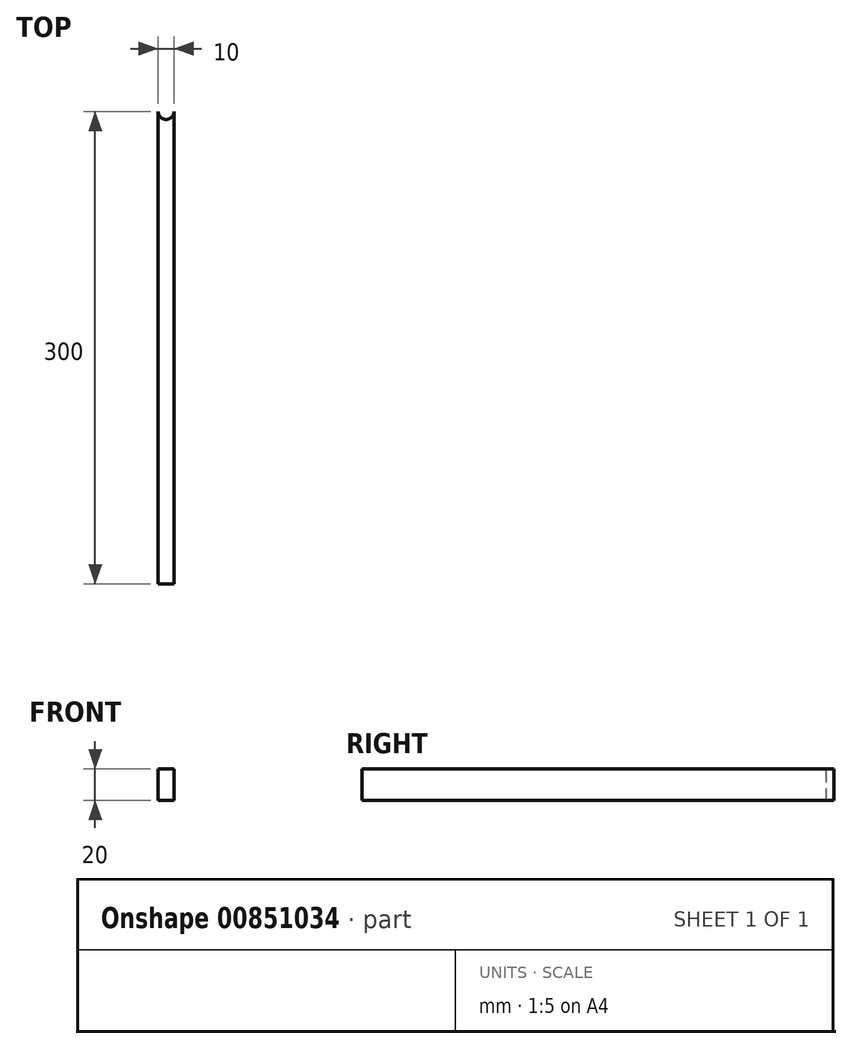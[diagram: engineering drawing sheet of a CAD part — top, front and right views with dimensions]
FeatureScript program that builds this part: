
annotation { "Feature Type Name" : "Feature", "Feature Type Description" : "" }
export const myFeature = defineFeature(function(context is Context, id is Id, definition is map)
    precondition{}
    {
        {
            var Q0;
            Q0=qCreatedBy(makeId("Front.planeOp"),FACE);
            var sketch = newSketch(context, id + "F0", { "sketchPlane" : qUnion([Q0])});
            skLineSegment(sketch, "E0.bottom", {"start": v(5, -10) * mm, "end": v(-5, -10) * mm});
            skLineSegment(sketch, "E0.top", {"start": v(5, 10) * mm, "end": v(-5, 10) * mm});
            skLineSegment(sketch, "E0.left", {"start": v(5, -10) * mm, "end": v(5, 10) * mm});
            skLineSegment(sketch, "E0.right", {"start": v(-5, -10) * mm, "end": v(-5, 10) * mm});
            skPoint(sketch, "E0.middle", {"position": v(0, 0) * mm});
            skSolve(sketch);
        }
        {
            var Q0;
            Q0=makeQuery(id+"F0.imprint","IMPRINT",FACE,{"disambiguationData":[TD([[makeQuery(id+"F0.imprint","IMPRINT",EDGE,{"derivedFrom":sQuery(id+"F0.wireOp",EDGE,"E0.bottom")}),-1.0]])]});
            extrude(context, id + "F1", {"entities" : qUnion([Q0]), "endBound" : BoundingType.SYMMETRIC, "oppositeDirection" : true, "depth" : 300 * mm, "offsetDistance" : 25 * mm});
        }
        {
            var Q0;
            Q0=makeQuery(id+"F1.opExtrude","SWEPT_FACE",FACE,{"disambiguationData":[OSD([sQuery(id+"F0.wireOp",EDGE,"E0.top")])]});
            var sketch = newSketch(context, id + "F2", { "sketchPlane" : qUnion([Q0])});
            skCircle(sketch, "E1", {"center": v(0, 150) * mm, "radius": 5 * mm});
            skSolve(sketch);
        }
        {
            var Q0;
            {var subQ1=sQuery(id+"F0.wireOp",EDGE,"E0.top");var subQ2=makeQuery(id+"F1.opExtrude","CAP_EDGE",EDGE,{"disambiguationData":[OSD([subQ1])],"isStart":false});Q0=makeQuery(id+"F2.imprint","IMPRINT",FACE,{"disambiguationData":[TD([[makeQuery(id+"F2.imprint","IMPRINT",EDGE,{"derivedFrom":subQ2}),-1.0]])]});}
            var Q1;
            {var subQ1=sQuery(id+"F0.wireOp",EDGE,"E0.top");var subQ2=makeQuery(id+"F1.opExtrude","CAP_EDGE",EDGE,{"disambiguationData":[OSD([subQ1])],"isStart":false});Q1=makeQuery(id+"F2.imprint","IMPRINT",FACE,{"disambiguationData":[TD([[makeQuery(id+"F2.imprint","IMPRINT",EDGE,{"derivedFrom":subQ2}),1.0]])]});}
            extrude(context, id + "F3", {"entities" : qUnion([Q0, Q1]), "operationType" : NewBodyOperationType.REMOVE, "endBound" : BoundingType.UP_TO_NEXT, "oppositeDirection" : true, "depth" : 25 * mm, "offsetDistance" : 25 * mm});
        }
    });
